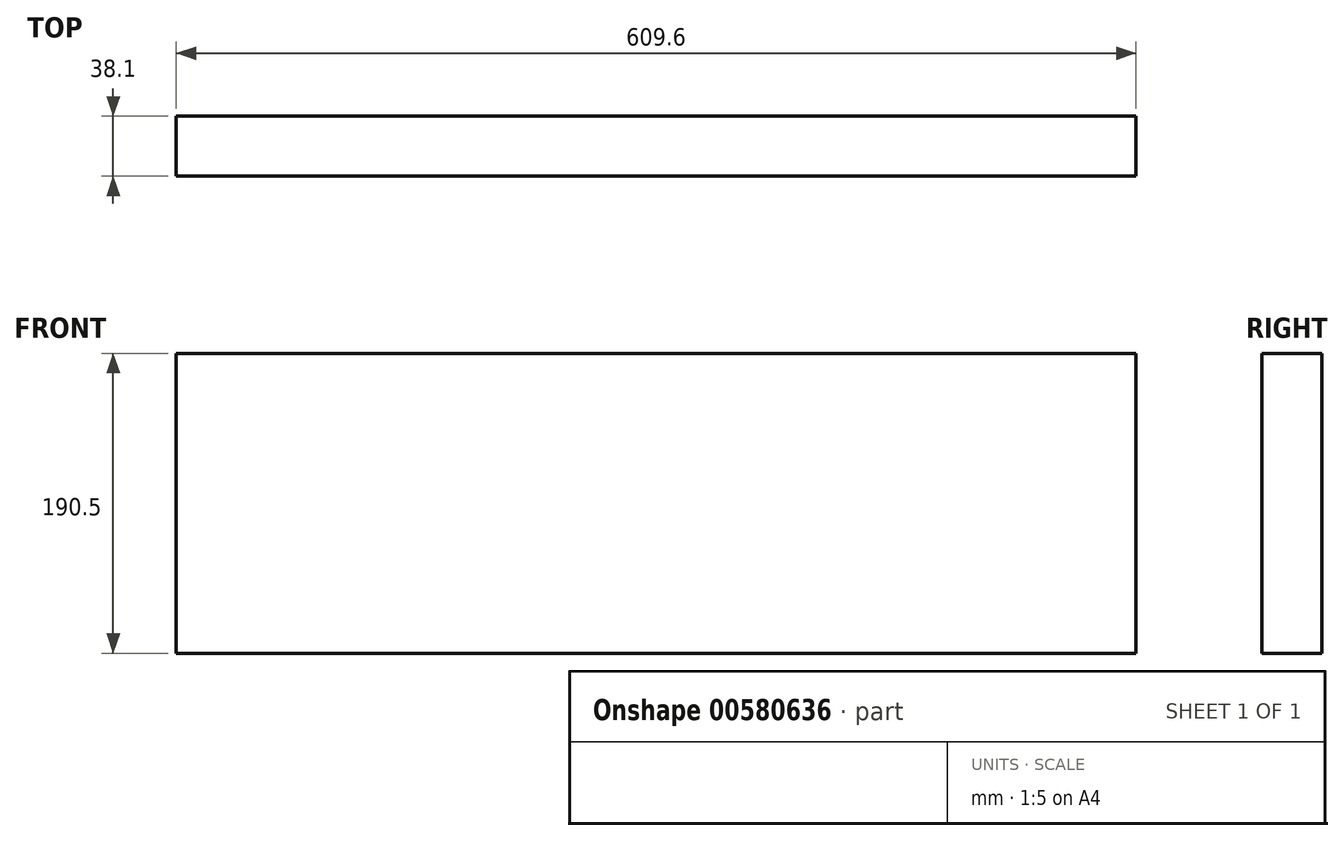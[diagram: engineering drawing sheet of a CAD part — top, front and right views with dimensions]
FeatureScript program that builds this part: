
annotation { "Feature Type Name" : "Feature", "Feature Type Description" : "" }
export const myFeature = defineFeature(function(context is Context, id is Id, definition is map)
    precondition{}
    {
        {
            var Q0;
            Q0=qCreatedBy(makeId("Top.planeOp"),FACE);
            var sketch = newSketch(context, id + "F0", { "sketchPlane" : qUnion([Q0])});
            skLineSegment(sketch, "E0.bottom", {"start": v(304.8, -19.05) * mm, "end": v(-304.8, -19.05) * mm});
            skLineSegment(sketch, "E0.top", {"start": v(304.8, 19.05) * mm, "end": v(-304.8, 19.05) * mm});
            skLineSegment(sketch, "E0.left", {"start": v(304.8, -19.05) * mm, "end": v(304.8, 19.05) * mm});
            skLineSegment(sketch, "E0.right", {"start": v(-304.8, -19.05) * mm, "end": v(-304.8, 19.05) * mm});
            skPoint(sketch, "E0.middle", {"position": v(0, 0) * mm});
            skSolve(sketch);
        }
        {
            var Q0;
            Q0 = qSketchRegion(id + "F0", true);
            extrude(context, id + "F1", {"entities" : qUnion([Q0]), "depth" : 190.5 * mm, "offsetDistance" : 25.4 * mm});
        }
    });
